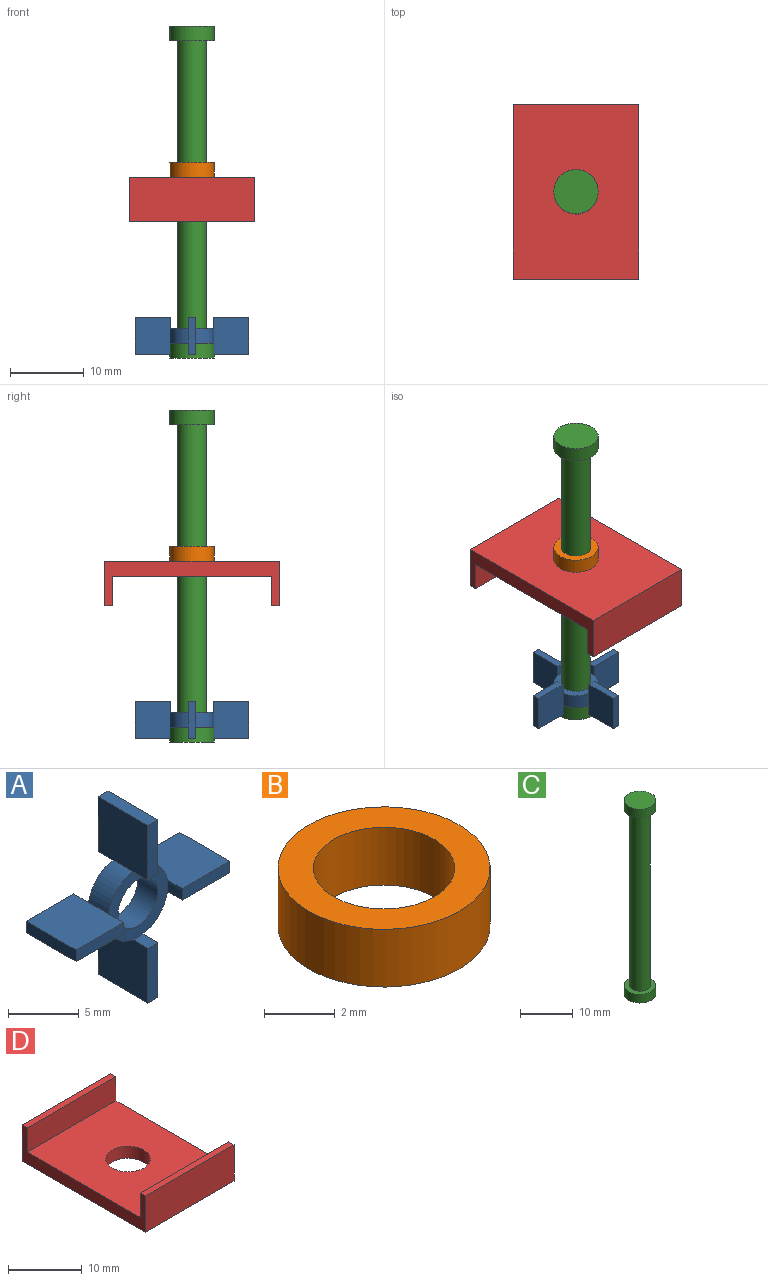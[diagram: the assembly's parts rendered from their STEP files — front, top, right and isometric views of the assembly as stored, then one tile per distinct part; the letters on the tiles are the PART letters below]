
ASSEMBLY  parts=4 mates=3
PART A: 35 faces, bbox 15.4x5x15.4 mm
  f0: cylinder r=3mm len=2.46mm, axis (0,1,0), area 7.4mm2, adj f5,f6,f22,f30
  f1: cylinder r=3mm len=2.46mm, axis (0,1,0), area 7.4mm2, adj f5,f6,f11,f24
  f2: cylinder r=3mm len=2.46mm, axis (0,1,0), area 7.4mm2, adj f5,f6,f16,f32
  f3: cylinder r=3mm len=2.46mm, axis (0,1,0), area 7.4mm2, adj f5,f6,f9,f18
  f4: cylinder r=2mm len=4mm, axis (0,1,0), area 25.1mm2, adj f5,f6
  f5: plane 6x6mm, normal (0,-1,0), area 15.7mm2, adj f0,f1,f2,f3,f4,f7,f14,f21
  f6: plane 6x6mm, normal (0,1,0), area 15.7mm2, adj f0,f1,f2,f3,f4,f8,f15,f23
  f7: cylinder r=3mm len=1.5mm, axis (0,1,0), area 1.5mm2, adj f5,f9,f11,f12
  f8: cylinder r=3mm len=1.5mm, axis (0,1,0), area 1.5mm2, adj f6,f9,f11,f13
  f9: plane 5x4.75mm, normal (-1,0,0), area 23.8mm2, adj f3,f7,f8,f10,f12,f13
  f10: plane 5x1mm, normal (0,0,-1), area 5mm2, adj f9,f11,f12,f13
  f11: plane 5x4.75mm, normal (1,0,0), area 23.8mm2, adj f1,f7,f8,f10,f12,f13
  f12: plane 4.75x1mm, normal (0,-1,0), area 4.7mm2, adj f7,f9,f10,f11
  f13: plane 4.75x1mm, normal (0,1,0), area 4.7mm2, adj f8,f9,f10,f11
  f14: cylinder r=3mm len=1.5mm, axis (0,1,0), area 1.5mm2, adj f5,f16,f18,f19
  f15: cylinder r=3mm len=1.5mm, axis (0,1,0), area 1.5mm2, adj f6,f16,f18,f20
  f16: plane 5x4.75mm, normal (0,0,1), area 23.7mm2, adj f2,f14,f15,f17,f19,f20
  f17: plane 5x1mm, normal (-1,0,0), area 5mm2, adj f16,f18,f19,f20
  f18: plane 5x4.75mm, normal (0,0,-1), area 23.7mm2, adj f3,f14,f15,f17,f19,f20
  f19: plane 4.75x1mm, normal (0,-1,0), area 4.7mm2, adj f14,f16,f17,f18
  f20: plane 4.75x1mm, normal (0,1,0), area 4.7mm2, adj f15,f16,f17,f18
  f21: cylinder r=3mm len=1.5mm, axis (0,1,0), area 1.5mm2, adj f5,f22,f24,f26
  f22: plane 5x4.75mm, normal (0,0,1), area 23.7mm2, adj f0,f21,f23,f25,f26,f27
  f23: cylinder r=3mm len=1.5mm, axis (0,1,0), area 1.5mm2, adj f6,f22,f24,f27
  f24: plane 5x4.75mm, normal (0,0,-1), area 23.7mm2, adj f1,f21,f23,f25,f26,f27
  f25: plane 5x1mm, normal (1,0,0), area 5mm2, adj f22,f24,f26,f27
  f26: plane 4.75x1mm, normal (0,-1,0), area 4.7mm2, adj f21,f22,f24,f25
  f27: plane 4.75x1mm, normal (0,1,0), area 4.7mm2, adj f22,f23,f24,f25
  f28: cylinder r=3mm len=1.5mm, axis (0,1,0), area 1.5mm2, adj f5,f30,f32,f33
  f29: cylinder r=3mm len=1.5mm, axis (0,1,0), area 1.5mm2, adj f6,f30,f32,f34
  f30: plane 5x4.75mm, normal (1,0,0), area 23.8mm2, adj f0,f28,f29,f31,f33,f34
  f31: plane 5x1mm, normal (0,0,1), area 5mm2, adj f30,f32,f33,f34
  f32: plane 5x4.75mm, normal (-1,0,0), area 23.8mm2, adj f2,f28,f29,f31,f33,f34
  f33: plane 4.75x1mm, normal (0,-1,0), area 4.7mm2, adj f28,f30,f31,f32
  f34: plane 4.75x1mm, normal (0,1,0), area 4.7mm2, adj f29,f30,f31,f32
PART B: 4 faces, bbox 6x6x2 mm
  f0: cylinder r=2mm len=4mm, axis (0,0,1), area 25.1mm2, adj f2,f3
  f1: cylinder r=3mm len=6mm, axis (0,0,1), area 37.7mm2, adj f2,f3
  f2: plane 6x6mm, normal (0,0,-1), area 15.7mm2, adj f0,f1
  f3: plane 6x6mm, normal (0,0,1), area 15.7mm2, adj f0,f1
PART C: 7 faces, bbox 6x6x45 mm
  f0: plane 6x6mm, normal (0,0,-1), area 28.3mm2, adj f1
  f1: cylinder r=3mm len=6mm, axis (0,0,-1), area 37.7mm2, adj f0,f2
  f2: plane 6x6mm, normal (0,0,1), area 16.3mm2, adj f1,f3
  f3: cylinder r=1.95mm len=41mm, axis (0,0,-1), area 502.3mm2, adj f2,f4
  f4: plane 6x6mm, normal (0,0,-1), area 16.3mm2, adj f3,f5
  f5: cylinder r=3mm len=6mm, axis (0,0,-1), area 37.7mm2, adj f4,f6
  f6: plane 6x6mm, normal (0,0,1), area 28.3mm2, adj f5
PART D: 11 faces, bbox 17x23.6x6 mm
  f0: plane 17x4mm, normal (0,-1,0), area 68mm2, adj f1,f3,f4,f7
  f1: plane 23.6x6mm, normal (1,0,0), area 55.2mm2, adj f0,f2,f4,f5,f7,f8,f9,f10
  f2: plane 17x6mm, normal (0,1,0), area 102mm2, adj f1,f3,f4,f5
  f3: plane 23.6x6mm, normal (-1,0,0), area 55.2mm2, adj f0,f2,f4,f5,f7,f8,f9,f10
  f4: plane 17x1mm, normal (0,0,1), area 17mm2, adj f0,f1,f2,f3
  f5: plane 23.6x17mm, normal (0,0,-1), area 372.9mm2, adj f1,f2,f3,f6,f9
  f6: cylinder r=3mm len=6mm, axis (0,0,-1), area 37.7mm2, adj f5,f7
  f7: plane 21.6x17mm, normal (0,0,1), area 338.9mm2, adj f0,f1,f3,f6,f8
  f8: plane 17x4mm, normal (0,1,0), area 68mm2, adj f1,f3,f7,f10
  f9: plane 17x6mm, normal (0,-1,0), area 102mm2, adj f1,f3,f5,f10
  f10: plane 17x1mm, normal (0,0,1), area 17mm2, adj f1,f3,f8,f9
PLACE A rot(axis=(-1,0,0),90deg) t=(-6.34,-3.9,-15.86)mm
PLACE B rot(axis=(1,0,0),180deg) t=(-6.34,-3.9,5.64)mm
PLACE C rot(axis=(1,0,0),180deg) t=(-6.34,-3.9,3.64)mm
PLACE D rot(axis=(1,0,0),180deg) t=(-6.34,-3.9,5.64)mm
MATE revolute A.f0 <-> C.f1  axis (0,0,-1) through (-6.34,-3.9,-16.86)mm
MATE fastened B.f0 <-> D.f6  axis (0,0,-1) through (-6.34,-3.9,5.64)mm
MATE fastened C.f1 <-> D.f6  axis (0,0,1) through (-6.34,-3.9,3.64)mm
